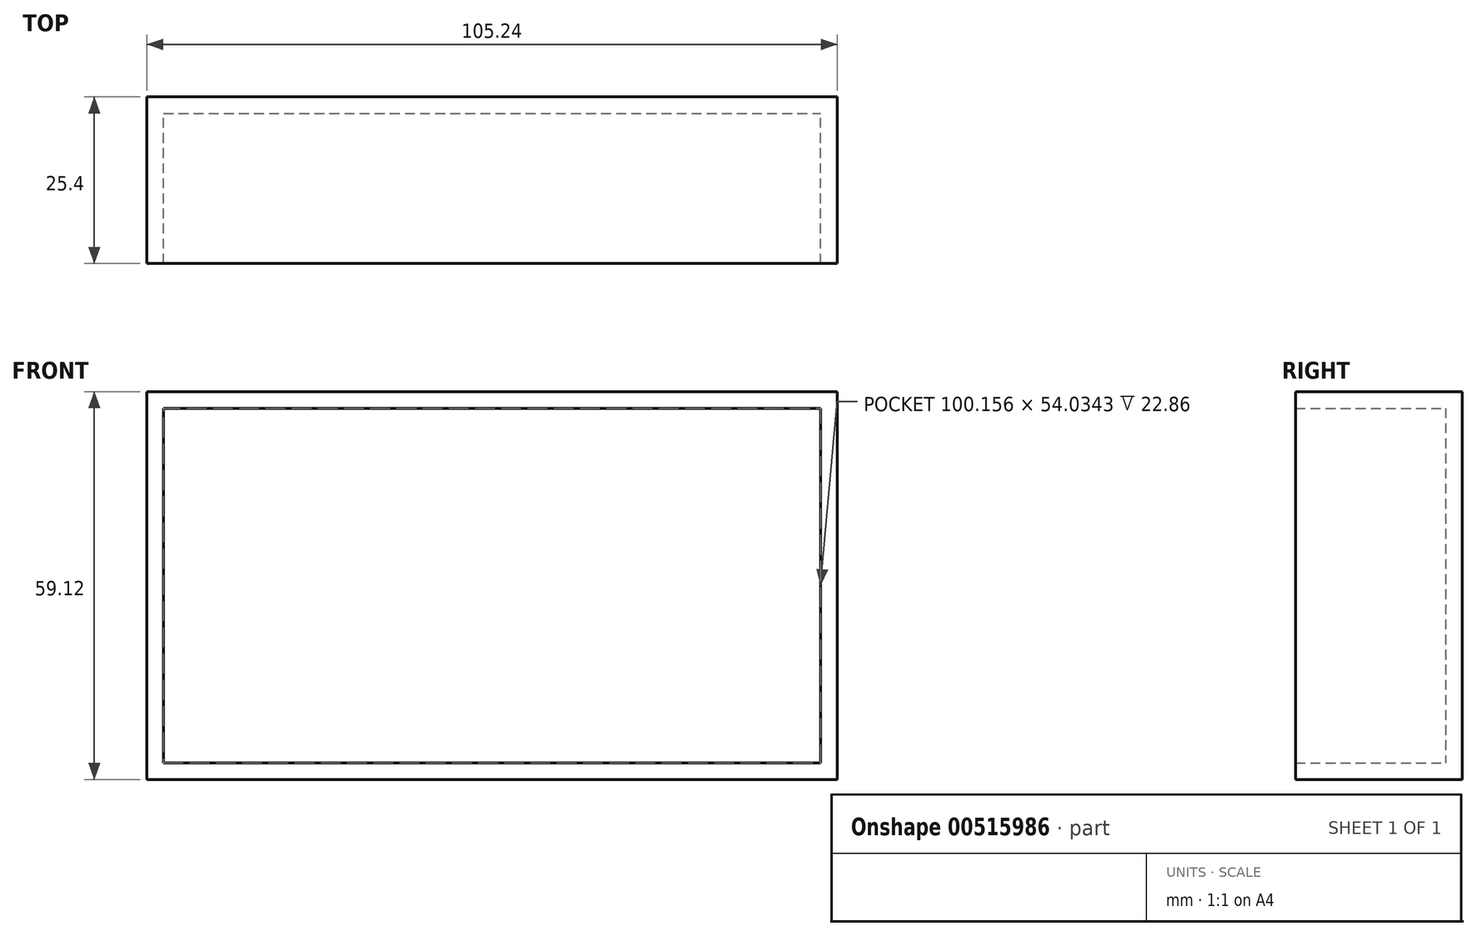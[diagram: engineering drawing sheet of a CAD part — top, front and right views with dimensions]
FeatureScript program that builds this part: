
annotation { "Feature Type Name" : "Feature", "Feature Type Description" : "" }
export const myFeature = defineFeature(function(context is Context, id is Id, definition is map)
    precondition{}
    {
        {
            var Q0;
            Q0=qCreatedBy(makeId("Front.planeOp"),FACE);
            var sketch = newSketch(context, id + "F0", { "sketchPlane" : qUnion([Q0])});
            skLineSegment(sketch, "E0.bottom", {"start": v(-52.08, 24.58) * mm, "end": v(53.16, 24.58) * mm});
            skLineSegment(sketch, "E0.top", {"start": v(-52.08, -34.54) * mm, "end": v(53.16, -34.54) * mm});
            skLineSegment(sketch, "E0.left", {"start": v(-52.08, 24.58) * mm, "end": v(-52.08, -34.54) * mm});
            skLineSegment(sketch, "E0.right", {"start": v(53.16, 24.58) * mm, "end": v(53.16, -34.54) * mm});
            skLineSegment(sketch, "E1", {"start": v(-32.8, 24.58) * mm, "end": v(-21.76, -34.54) * mm});
            skSolve(sketch);
        }
        {
            var Q0;
            Q0=makeQuery(id+"F0.imprint","IMPRINT",FACE,{"disambiguationData":[TD([[makeQuery(id+"F0.imprint","IMPRINT",EDGE,{"derivedFrom":sQuery(id+"F0.wireOp",EDGE,"E0.bottom")}),-1.0]])]});
            extrude(context, id + "F1", {"entities" : qUnion([Q0]), "depth" : 25.4 * mm, "offsetDistance" : 25.4 * mm});
        }
        {
            var Q0;
            Q0=makeQuery(id+"F1.opExtrude","CAP_FACE",FACE,{"disambiguationData":[OSD([sQuery(id+"F0.wireOp",EDGE,"E0.bottom"),sQuery(id+"F0.wireOp",EDGE,"E0.top"),sQuery(id+"F0.wireOp",EDGE,"E0.left"),sQuery(id+"F0.wireOp",EDGE,"E0.right")])],"isStart":false});
            shell(context, id + "F2", {"entities" : qUnion([Q0]), "thickness" : 2.54 * mm});
        }
    });
